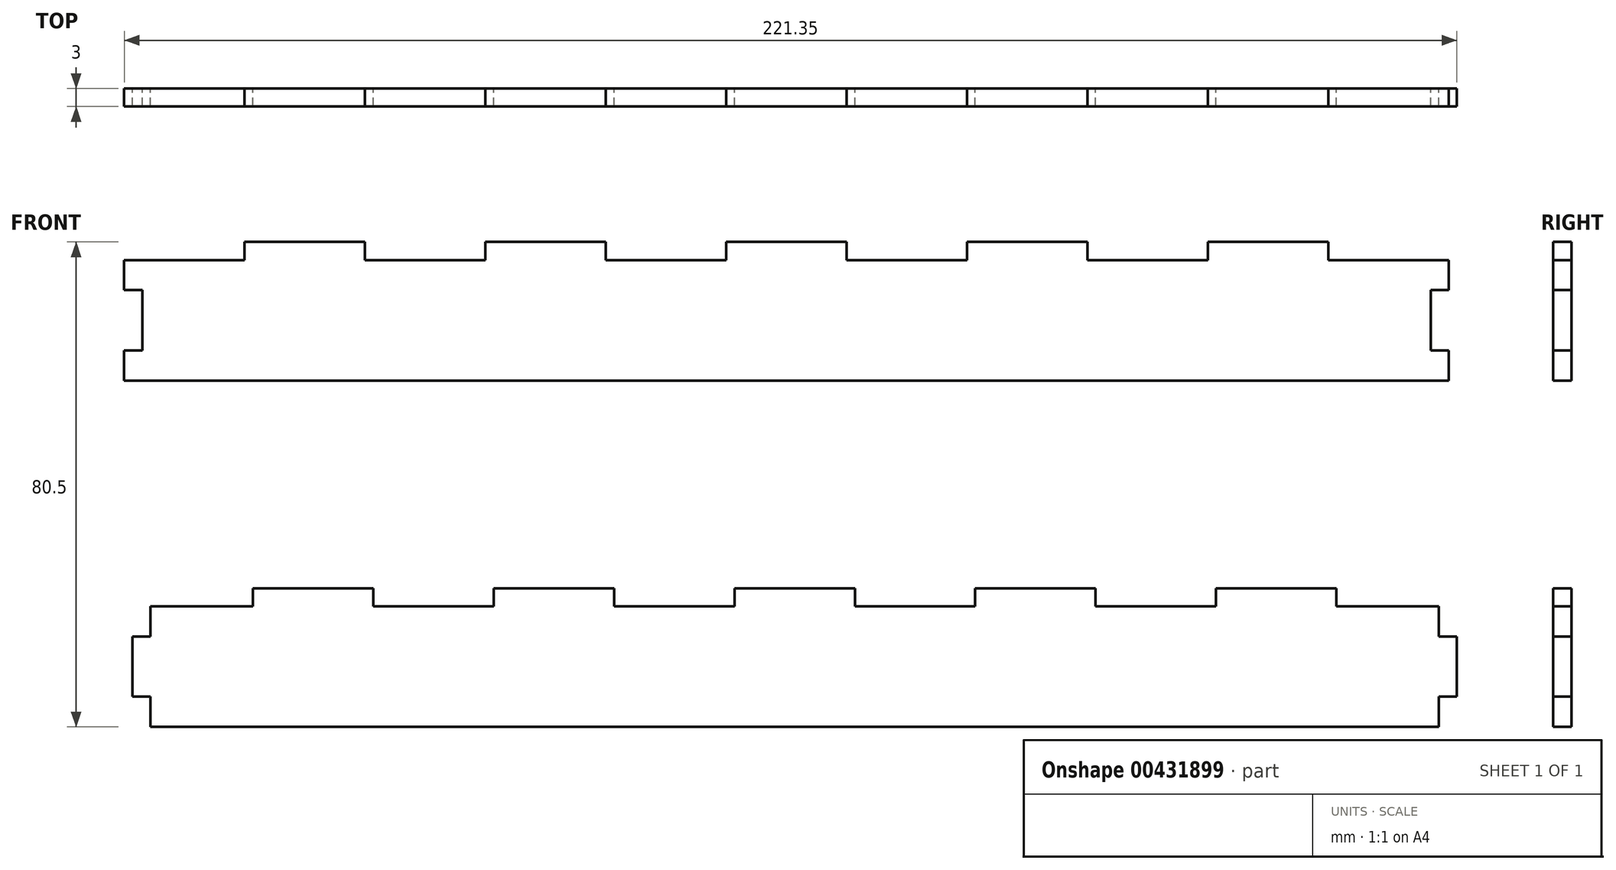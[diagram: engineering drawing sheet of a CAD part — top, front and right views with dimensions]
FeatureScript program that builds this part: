
annotation { "Feature Type Name" : "Feature", "Feature Type Description" : "" }
export const myFeature = defineFeature(function(context is Context, id is Id, definition is map)
    precondition{}
    {
        {
            var Q0;
            Q0=qCreatedBy(makeId("Front.planeOp"),FACE);
            var sketch = newSketch(context, id + "F0", { "sketchPlane" : qUnion([Q0])});
            skLineSegment(sketch, "E0.bottom", {"start": v(-107, 10) * mm, "end": v(-90, 10) * mm});
            skLineSegment(sketch, "E0.top", {"start": v(-107, -10) * mm, "end": v(107, -10) * mm});
            skLineSegment(sketch, "E0.left", {"start": v(-107, 10) * mm, "end": v(-107, 5) * mm});
            skLineSegment(sketch, "E0.right", {"start": v(107, 10) * mm, "end": v(107, 5) * mm});
            skPoint(sketch, "E0.middle", {"position": v(0, 0) * mm});
            skLineSegment(sketch, "E1.bottom", {"start": v(-10, 13) * mm, "end": v(10, 13) * mm});
            skLineSegment(sketch, "E1.left", {"start": v(-10, 13) * mm, "end": v(-10, 10) * mm});
            skLineSegment(sketch, "E1.right", {"start": v(10, 13) * mm, "end": v(10, 10) * mm});
            skPoint(sketch, "E1.middle", {"position": v(0, 10) * mm});
            skLineSegment(sketch, "E2.bottom", {"start": v(-50, 13) * mm, "end": v(-30, 13) * mm});
            skLineSegment(sketch, "E2.left", {"start": v(-50, 13) * mm, "end": v(-50, 10) * mm});
            skLineSegment(sketch, "E2.right", {"start": v(-30, 13) * mm, "end": v(-30, 10) * mm});
            skPoint(sketch, "E2.middle", {"position": v(-40, 10) * mm});
            skLineSegment(sketch, "E3.bottom", {"start": v(30, 13) * mm, "end": v(50, 13) * mm});
            skLineSegment(sketch, "E3.left", {"start": v(30, 13) * mm, "end": v(30, 10) * mm});
            skLineSegment(sketch, "E3.right", {"start": v(50, 13) * mm, "end": v(50, 10) * mm});
            skPoint(sketch, "E3.middle", {"position": v(40, 10) * mm});
            skLineSegment(sketch, "E4.bottom", {"start": v(70, 13) * mm, "end": v(90, 13) * mm});
            skLineSegment(sketch, "E4.left", {"start": v(70, 13) * mm, "end": v(70, 10) * mm});
            skLineSegment(sketch, "E4.right", {"start": v(90, 13) * mm, "end": v(90, 10) * mm});
            skPoint(sketch, "E4.middle", {"position": v(80, 10) * mm});
            skLineSegment(sketch, "E5.bottom", {"start": v(-90, 13) * mm, "end": v(-70, 13) * mm});
            skLineSegment(sketch, "E5.left", {"start": v(-90, 13) * mm, "end": v(-90, 10) * mm});
            skLineSegment(sketch, "E5.right", {"start": v(-70, 13) * mm, "end": v(-70, 10) * mm});
            skPoint(sketch, "E5.middle", {"position": v(-80, 10) * mm});
            skLineSegment(sketch, "E6.trimOffspring", {"start": v(-70, 10) * mm, "end": v(-50, 10) * mm});
            skPoint(sketch, "E7.orphan", {"position": v(-70, 7) * mm});
            skPoint(sketch, "E8.orphan", {"position": v(-90, 7) * mm});
            skPoint(sketch, "E2.top.start.orphan", {"position": v(-50, 7) * mm});
            skLineSegment(sketch, "E9.trimOffspring", {"start": v(-30, 10) * mm, "end": v(-10, 10) * mm});
            skPoint(sketch, "E10.orphan", {"position": v(-30, 7) * mm});
            skLineSegment(sketch, "E11.trimOffspring", {"start": v(10, 10) * mm, "end": v(30, 10) * mm});
            skPoint(sketch, "E1.top.end.orphan", {"position": v(10, 7) * mm});
            skPoint(sketch, "E12.orphan", {"position": v(-10, 7) * mm});
            skLineSegment(sketch, "E13.trimOffspring", {"start": v(50, 10) * mm, "end": v(70, 10) * mm});
            skPoint(sketch, "E14.orphan", {"position": v(50, 7) * mm});
            skPoint(sketch, "E15.orphan", {"position": v(30, 7) * mm});
            skPoint(sketch, "E16.orphan", {"position": v(70, 7) * mm});
            skLineSegment(sketch, "E17.trimOffspring", {"start": v(90, 10) * mm, "end": v(107, 10) * mm});
            skPoint(sketch, "E18.orphan", {"position": v(90, 7) * mm});
            skLineSegment(sketch, "E19.bottom", {"start": v(-107, 5) * mm, "end": v(-110, 5) * mm});
            skLineSegment(sketch, "E19.top", {"start": v(-107, -5) * mm, "end": v(-110, -5) * mm});
            skLineSegment(sketch, "E19.right", {"start": v(-110, 5) * mm, "end": v(-110, -5) * mm});
            skPoint(sketch, "E19.middle", {"position": v(-107, 0) * mm});
            skPoint(sketch, "E20.orphan", {"position": v(-104, 5) * mm});
            skLineSegment(sketch, "E21.trimOffspring", {"start": v(-107, -5) * mm, "end": v(-107, -10) * mm});
            skPoint(sketch, "E22.orphan", {"position": v(-104, -5) * mm});
            skLineSegment(sketch, "E23.bottom", {"start": v(107, 5) * mm, "end": v(110, 5) * mm});
            skLineSegment(sketch, "E23.top", {"start": v(107, -5) * mm, "end": v(110, -5) * mm});
            skLineSegment(sketch, "E23.right", {"start": v(110, 5) * mm, "end": v(110, -5) * mm});
            skPoint(sketch, "E23.middle", {"position": v(107, 0) * mm});
            skPoint(sketch, "E24.orphan", {"position": v(104, 5) * mm});
            skPoint(sketch, "E25.orphan", {"position": v(104, -5) * mm});
            skLineSegment(sketch, "E26.trimOffspring", {"start": v(107, -5) * mm, "end": v(107, -10) * mm});
            skLineSegment(sketch, "E27.bottom", {"start": v(-111.35, 67.5) * mm, "end": v(-91.35, 67.5) * mm});
            skLineSegment(sketch, "E27.top", {"start": v(-111.35, 47.5) * mm, "end": v(108.65, 47.5) * mm});
            skLineSegment(sketch, "E27.left", {"start": v(-111.35, 67.5) * mm, "end": v(-111.35, 62.5) * mm});
            skLineSegment(sketch, "E27.right", {"start": v(108.65, 67.5) * mm, "end": v(108.65, 62.5) * mm});
            skPoint(sketch, "E27.middle", {"position": v(-1.35, 57.5) * mm});
            skLineSegment(sketch, "E28.bottom", {"start": v(-11.35, 70.5) * mm, "end": v(8.65, 70.5) * mm});
            skLineSegment(sketch, "E28.left", {"start": v(-11.35, 70.5) * mm, "end": v(-11.35, 67.5) * mm});
            skLineSegment(sketch, "E28.right", {"start": v(8.65, 70.5) * mm, "end": v(8.65, 67.5) * mm});
            skPoint(sketch, "E28.middle", {"position": v(-1.35, 67.5) * mm});
            skLineSegment(sketch, "E29.bottom", {"start": v(-51.35, 70.5) * mm, "end": v(-31.35, 70.5) * mm});
            skLineSegment(sketch, "E29.left", {"start": v(-51.35, 70.5) * mm, "end": v(-51.35, 67.5) * mm});
            skLineSegment(sketch, "E29.right", {"start": v(-31.35, 70.5) * mm, "end": v(-31.35, 67.5) * mm});
            skPoint(sketch, "E29.middle", {"position": v(-41.35, 67.5) * mm});
            skLineSegment(sketch, "E30.bottom", {"start": v(28.65, 70.5) * mm, "end": v(48.65, 70.5) * mm});
            skLineSegment(sketch, "E30.left", {"start": v(28.65, 70.5) * mm, "end": v(28.65, 67.5) * mm});
            skLineSegment(sketch, "E30.right", {"start": v(48.65, 70.5) * mm, "end": v(48.65, 67.5) * mm});
            skPoint(sketch, "E30.middle", {"position": v(38.65, 67.5) * mm});
            skLineSegment(sketch, "E31.bottom", {"start": v(68.65, 70.5) * mm, "end": v(88.65, 70.5) * mm});
            skLineSegment(sketch, "E31.left", {"start": v(68.65, 70.5) * mm, "end": v(68.65, 67.5) * mm});
            skLineSegment(sketch, "E31.right", {"start": v(88.65, 70.5) * mm, "end": v(88.65, 67.5) * mm});
            skPoint(sketch, "E31.middle", {"position": v(78.65, 67.5) * mm});
            skLineSegment(sketch, "E32.bottom", {"start": v(-91.35, 70.5) * mm, "end": v(-71.35, 70.5) * mm});
            skLineSegment(sketch, "E32.left", {"start": v(-91.35, 70.5) * mm, "end": v(-91.35, 67.5) * mm});
            skLineSegment(sketch, "E32.right", {"start": v(-71.35, 70.5) * mm, "end": v(-71.35, 67.5) * mm});
            skPoint(sketch, "E32.middle", {"position": v(-81.35, 67.5) * mm});
            skLineSegment(sketch, "E33.trimOffspring", {"start": v(-71.35, 67.5) * mm, "end": v(-51.35, 67.5) * mm});
            skPoint(sketch, "E34.orphan", {"position": v(-71.35, 64.5) * mm});
            skPoint(sketch, "E35.orphan", {"position": v(-91.35, 64.5) * mm});
            skPoint(sketch, "E29.top.start.orphan", {"position": v(-51.35, 64.5) * mm});
            skLineSegment(sketch, "E36.trimOffspring", {"start": v(-31.35, 67.5) * mm, "end": v(-11.35, 67.5) * mm});
            skPoint(sketch, "E37.orphan", {"position": v(-31.35, 64.5) * mm});
            skLineSegment(sketch, "E38.trimOffspring", {"start": v(8.65, 67.5) * mm, "end": v(28.65, 67.5) * mm});
            skPoint(sketch, "E28.top.end.orphan", {"position": v(8.65, 64.5) * mm});
            skPoint(sketch, "E39.orphan", {"position": v(-11.35, 64.5) * mm});
            skLineSegment(sketch, "E40.trimOffspring", {"start": v(48.65, 67.5) * mm, "end": v(68.65, 67.5) * mm});
            skPoint(sketch, "E41.orphan", {"position": v(48.65, 64.5) * mm});
            skPoint(sketch, "E42.orphan", {"position": v(28.65, 64.5) * mm});
            skPoint(sketch, "E43.orphan", {"position": v(68.65, 64.5) * mm});
            skLineSegment(sketch, "E44.trimOffspring", {"start": v(88.65, 67.5) * mm, "end": v(108.65, 67.5) * mm});
            skPoint(sketch, "E45.orphan", {"position": v(88.65, 64.5) * mm});
            skPoint(sketch, "E46.middle", {"position": v(-111.35, 57.5) * mm});
            skPoint(sketch, "E47.orphan", {"position": v(-108.35, 62.5) * mm});
            skLineSegment(sketch, "E48.trimOffspring", {"start": v(-111.35, 52.5) * mm, "end": v(-111.35, 47.5) * mm});
            skPoint(sketch, "E49.orphan", {"position": v(-108.35, 52.5) * mm});
            skPoint(sketch, "E50.middle", {"position": v(108.65, 57.5) * mm});
            skPoint(sketch, "E51.orphan", {"position": v(105.65, 62.5) * mm});
            skPoint(sketch, "E52.orphan", {"position": v(105.65, 52.5) * mm});
            skLineSegment(sketch, "E53.trimOffspring", {"start": v(108.65, 52.5) * mm, "end": v(108.65, 47.5) * mm});
            skLineSegment(sketch, "E54.bottom", {"start": v(105.65, 62.5) * mm, "end": v(108.65, 62.5) * mm});
            skLineSegment(sketch, "E54.top", {"start": v(105.65, 52.5) * mm, "end": v(108.65, 52.5) * mm});
            skLineSegment(sketch, "E54.left", {"start": v(105.65, 62.5) * mm, "end": v(105.65, 52.5) * mm});
            skPoint(sketch, "E50.top.end.orphan", {"position": v(111.65, 52.5) * mm});
            skLineSegment(sketch, "E55.bottom", {"start": v(-111.35, 62.5) * mm, "end": v(-108.35, 62.5) * mm});
            skLineSegment(sketch, "E55.top", {"start": v(-111.35, 52.5) * mm, "end": v(-108.35, 52.5) * mm});
            skLineSegment(sketch, "E55.right", {"start": v(-108.35, 62.5) * mm, "end": v(-108.35, 52.5) * mm});
            skPoint(sketch, "E46.top.end.orphan", {"position": v(-114.35, 52.5) * mm});
            skPoint(sketch, "E56.orphan", {"position": v(-114.35, 62.5) * mm});
            skSolve(sketch);
        }
        {
            var Q0;
            Q0=makeQuery(id+"F0.imprint","IMPRINT",FACE,{"disambiguationData":[TD([[makeQuery(id+"F0.imprint","IMPRINT",EDGE,{"derivedFrom":sQuery(id+"F0.wireOp",EDGE,"E27.bottom")}),-1.0]])]});
            var Q1;
            Q1=makeQuery(id+"F0.imprint","IMPRINT",FACE,{"disambiguationData":[TD([[makeQuery(id+"F0.imprint","IMPRINT",EDGE,{"derivedFrom":sQuery(id+"F0.wireOp",EDGE,"E0.bottom")}),-1.0]])]});
            extrude(context, id + "F1", {"entities" : qUnion([Q0, Q1]), "depth" : 3 * mm});
        }
    });
